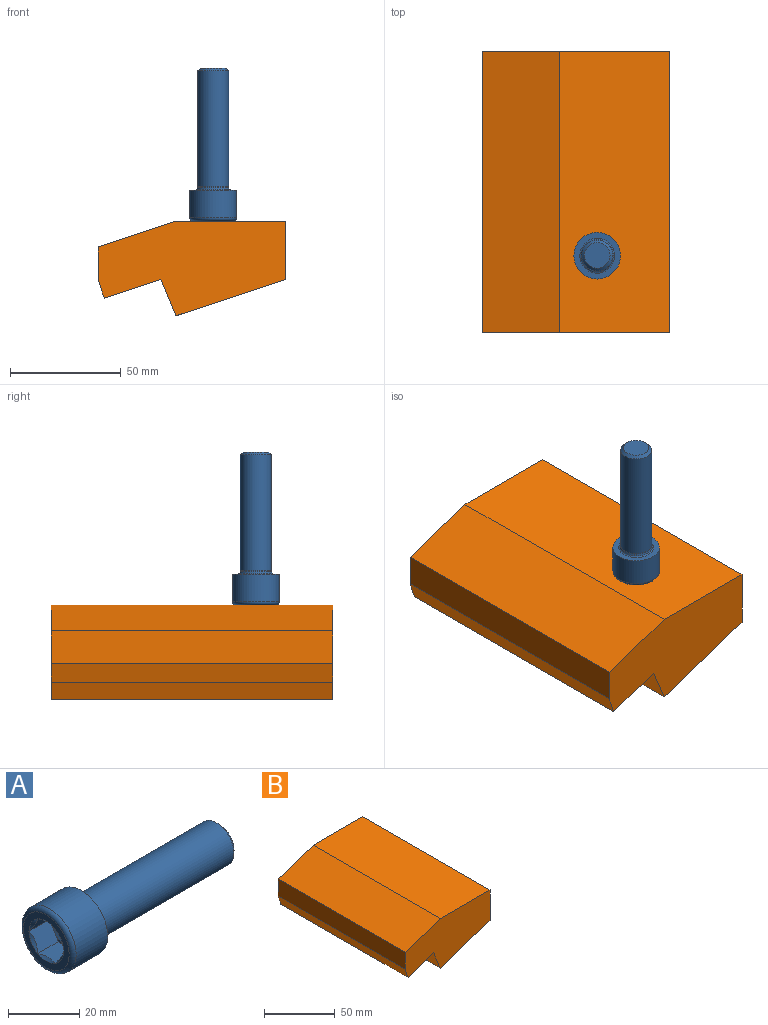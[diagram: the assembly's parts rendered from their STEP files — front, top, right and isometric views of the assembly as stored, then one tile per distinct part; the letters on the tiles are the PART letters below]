
ASSEMBLY  parts=2 mates=1
PART A: 29 faces, bbox 69x22.7x22.7 mm
  f0: cone r=3mm half-angle=60deg, axis (-1,0,0), area 130.6mm2, adj f13,f14,f15,f16,f17,f18
  f1: torus R=9.1mm, axis (-1,0,0), area 138.1mm2, adj f2,f25
  f2: cylinder r=10.5mm len=21mm, axis (-1,0,0), area 831.3mm2, adj f1,f27
  f3: torus R=7.85mm, axis (-1,0,0), area 36.4mm2, adj f4,f27
  f4: cone r=7.15mm half-angle=16.4deg, axis (-1,0,0), area 39.8mm2, adj f3,f5
  f5: torus R=7.6mm, axis (-1,0,0), area 7.6mm2, adj f4,f6
  f6: cylinder r=7mm len=52.32mm, axis (-1,0,0), area 2301.3mm2, adj f5,f7
  f7: cone r=6.39mm half-angle=45deg, axis (-1,0,0), area 69.6mm2, adj f6,f26
  f8: plane 8.2x6mm, normal (0,0.87,0.5), area 52.9mm2, adj f9,f10,f15,f16,f25,f28
  f9: plane 8.2x6.93mm, normal (0,0,1), area 52.9mm2, adj f8,f11,f14,f15,f24,f25
  f10: plane 8.2x6mm, normal (0,0.87,-0.5), area 52.9mm2, adj f8,f12,f16,f17,f23,f25
  f11: plane 8.2x6mm, normal (0,-0.87,0.5), area 52.9mm2, adj f9,f13,f14,f19,f22,f25
  f12: plane 8.2x6.93mm, normal (0,0,-1), area 52.9mm2, adj f10,f17,f18,f19,f21,f25
  f13: plane 6x1.73mm, normal (-1,0,0), area 1.9mm2, adj f0,f11,f19
  f14: plane 5.2x3mm, normal (-1,0,0), area 1.9mm2, adj f0,f9,f11
  f15: plane 5.2x3mm, normal (-1,0,0), area 1.9mm2, adj f0,f8,f9
  f16: plane 6x1.73mm, normal (-1,0,0), area 1.9mm2, adj f0,f8,f10
  f17: plane 5.2x3mm, normal (-1,0,0), area 1.9mm2, adj f0,f10,f12
  f18: plane 5.2x3mm, normal (-1,0,0), area 1.9mm2, adj f0,f12,f19
  f19: plane 8.2x6mm, normal (0,-0.87,-0.5), area 52.9mm2, adj f11,f12,f13,f18,f20,f25
  f20: cone r=6.44mm half-angle=45deg, axis (-1,0,0), area 5.7mm2, adj f19,f25
  f21: cone r=6.44mm half-angle=45deg, axis (-1,0,0), area 5.7mm2, adj f12,f25
  f22: cone r=6.44mm half-angle=45deg, axis (-1,0,0), area 5.7mm2, adj f11,f25
  f23: cone r=6.44mm half-angle=45deg, axis (-1,0,0), area 5.7mm2, adj f10,f25
  f24: cone r=6.44mm half-angle=45deg, axis (-1,0,0), area 5.7mm2, adj f9,f25
  f25: plane 18.2x18.2mm, normal (-1,0,0), area 111.1mm2, adj f1,f8,f9,f10,f11,f12,f19,f20
  f26: plane 11.55x11.55mm, normal (1,0,0), area 104.7mm2, adj f7
  f27: plane 21x21mm, normal (1,0,0), area 152.8mm2, adj f2,f3
  f28: cone r=6.44mm half-angle=45deg, axis (-1,0,0), area 5.7mm2, adj f8,f25
PART B: 18 faces, bbox 84.6x127x42.8 mm
  f0: plane 127x16.48mm, normal (-0.93,0,-0.38), area 2260.8mm2, adj f1,f7,f8,f9
  f1: plane 127x49.59mm, normal (0.32,0,-0.95), area 782.7mm2, adj f0,f2,f8,f9,f10,f11,f17
  f2: plane 127x26.3mm, normal (1,0,0), area 3340.1mm2, adj f1,f3,f8,f9
  f3: plane 127x49.59mm, normal (0,0,1), area 6298mm2, adj f2,f4,f8,f9
  f4: plane 127x35.04mm, normal (-0.32,0,0.95), area 4689.7mm2, adj f3,f5,f8,f9
  f5: plane 127x14.66mm, normal (-1,0,0), area 1861.4mm2, adj f4,f6,f8,f9
  f6: plane 127x8.47mm, normal (-0.95,0,-0.32), area 1133.5mm2, adj f5,f7,f8,f9
  f7: plane 127x25.49mm, normal (0.32,0,-0.95), area 3411.5mm2, adj f0,f6,f8,f9
  f8: plane 84.63x42.78mm, normal (0,-1,0), area 2605.8mm2, adj f0,f1,f2,f3,f4,f5,f6,f7
  f9: plane 84.63x42.78mm, normal (0,1,0), area 447.6mm2, adj f0,f1,f2,f3,f4,f5,f6,f7
  f10: plane 124.46x18.83mm, normal (0.93,0,0.38), area 2532.4mm2, adj f1,f9,f16,f17
  f11: plane 124.46x24.6mm, normal (-1,0,0), area 3062.2mm2, adj f1,f9,f12,f17
  f12: plane 124.46x46.64mm, normal (0,0,-1), area 5804.7mm2, adj f9,f11,f13,f17
  f13: plane 124.46x32.91mm, normal (0.32,0,-0.95), area 4316.7mm2, adj f9,f12,f14,f17
  f14: plane 124.46x12.41mm, normal (1,0,0), area 1544.9mm2, adj f9,f13,f15,f17
  f15: plane 124.46x5.67mm, normal (0.95,0,0.32), area 743.6mm2, adj f9,f14,f16,f17
  f16: plane 124.46x25.34mm, normal (-0.32,0,0.95), area 3322.7mm2, adj f9,f10,f15,f17
  f17: plane 79.55x39.44mm, normal (0,1,0), area 2158.2mm2, adj f1,f10,f11,f12,f13,f14,f15,f16
PLACE A rot(axis=(0.71,0,0.71),180deg) t=(-17.5,-56.44,-23.81)mm
PLACE B t=(-34.34,35.84,-80.58)mm
MATE planar A.f25 <-> B.f3  axis (0,0,-1) through (-17.54,-49.54,-37.81)mm
